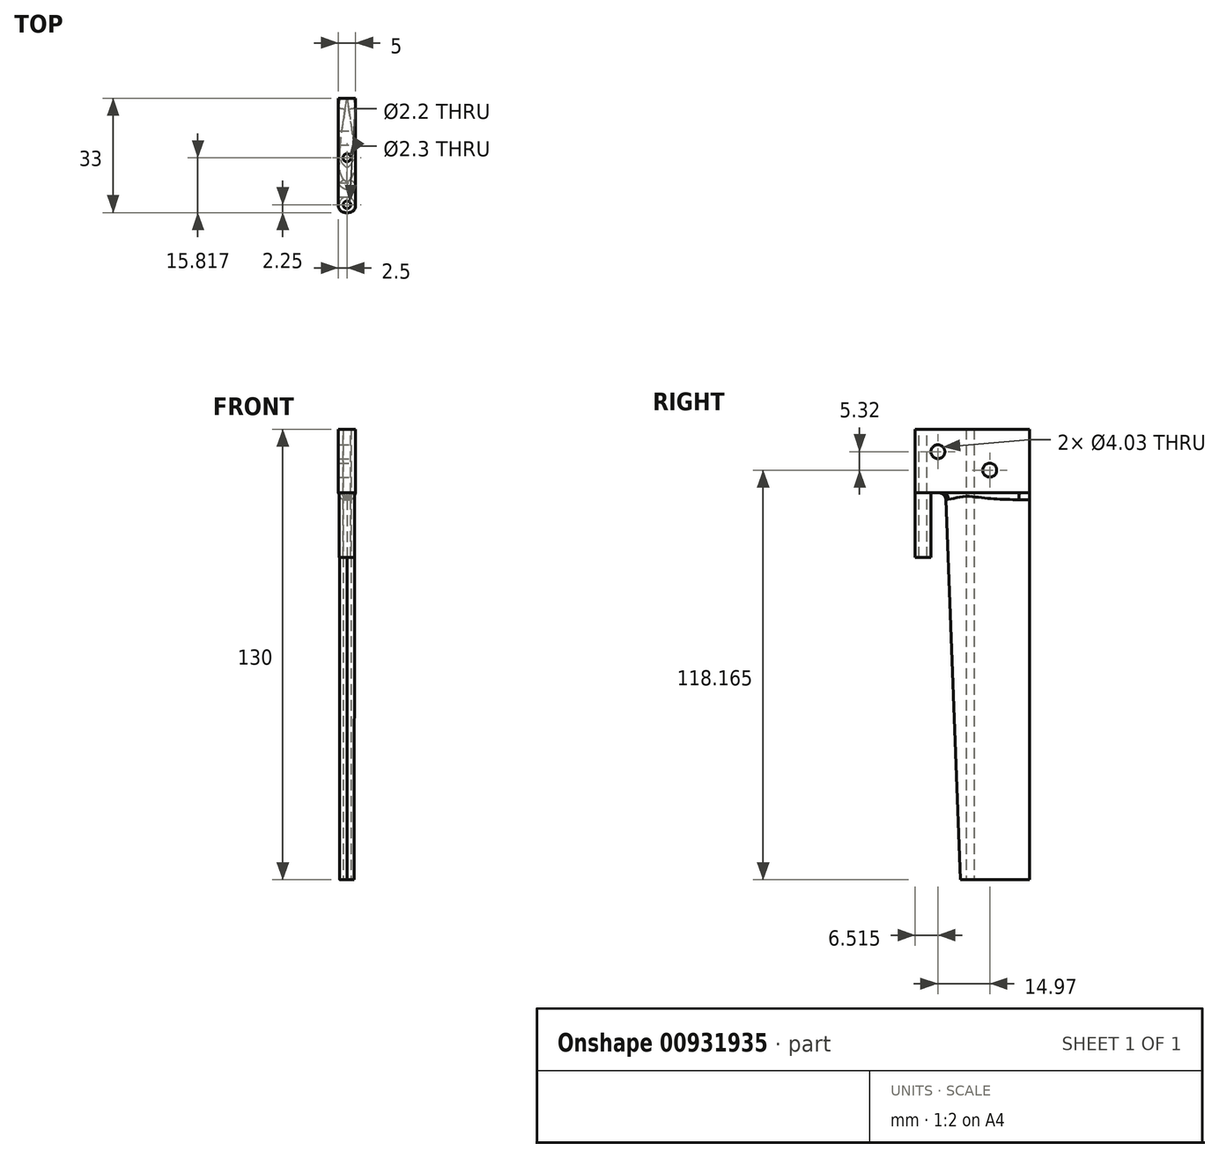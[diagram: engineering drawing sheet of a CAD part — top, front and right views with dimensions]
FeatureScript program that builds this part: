
annotation { "Feature Type Name" : "Feature", "Feature Type Description" : "" }
export const myFeature = defineFeature(function(context is Context, id is Id, definition is map)
    precondition{}
    {
        {
            var Q0;
            Q0=qCreatedBy(makeId("Top.planeOp"),FACE);
            var sketch = newSketch(context, id + "F0", { "sketchPlane" : qUnion([Q0])});
            skLineSegment(sketch, "E0", {"start": v(0, 0) * mm, "end": v(0, 20) * mm, "construction": true});
            skFitSpline(sketch, "E1", {"points": [v(0, 0) * mm, v(1.82, 2.47) * mm, v(1.18, 12.7) * mm, v(0, 20) * mm], "startDerivative": vector(9.05, 2.42) * mm, "endDerivative": vector(-3.34, 17.34) * mm});
            skFitSpline(sketch, "E2.MirrorCS", {"points": [v(0, 0) * mm, v(-1.82, 2.47) * mm, v(-1.18, 12.7) * mm, v(0, 20) * mm], "startDerivative": vector(-9.05, 2.42) * mm, "endDerivative": vector(3.34, 17.34) * mm});
            skLineSegment(sketch, "E3", {"start": v(-1.82, 2.47) * mm, "end": v(1.82, 2.47) * mm, "construction": true});
            skSolve(sketch);
        }
        {
            var Q0;
            Q0=qCreatedBy(makeId("Top.planeOp"),FACE);
            cPlane(context, id + "F1", {"entities" : qUnion([Q0]), "cplaneType" : CPlaneType.OFFSET, "offset" : 130 * mm, "width" : 150 * mm, "height" : 150 * mm});
        }
        {
            var Q0;
            Q0=qCreatedBy(id+"F1.planeOp",FACE);
            var sketch = newSketch(context, id + "F2", { "sketchPlane" : qUnion([Q0])});
            skLineSegment(sketch, "E4", {"start": v(0, 0) * mm, "end": v(0, -5) * mm, "construction": true});
            skFitSpline(sketch, "E5", {"points": [v(0, -5) * mm, v(2.11, -0.7) * mm, v(1.9, 6.2) * mm, v(0, 20) * mm], "startDerivative": vector(16.45, 7.84) * mm, "endDerivative": vector(-5.95, 33.02) * mm});
            skFitSpline(sketch, "E6.MirrorCS", {"points": [v(0, -5) * mm, v(-2.11, -0.7) * mm, v(-1.9, 6.2) * mm, v(0, 20) * mm], "startDerivative": vector(-16.45, 7.84) * mm, "endDerivative": vector(5.95, 33.02) * mm});
            skLineSegment(sketch, "E7", {"start": v(0, 0) * mm, "end": v(0, 20) * mm, "construction": true});
            skSolve(sketch);
        }
        {
            var Q0;
            Q0=qCreatedBy(id+"F1.planeOp",FACE);
            var sketch = newSketch(context, id + "F3", { "sketchPlane" : qUnion([Q0])});
            skPoint(sketch, "E8.middle", {"position": v(0, 0) * mm});
            skLineSegment(sketch, "E9", {"start": v(0, 0) * mm, "end": v(0, 20) * mm, "construction": true});
            skLineSegment(sketch, "E10", {"start": v(0, 20) * mm, "end": v(2.5, 20) * mm});
            skLineSegment(sketch, "E11", {"start": v(0, 20) * mm, "end": v(-2.5, 20) * mm});
            skLineSegment(sketch, "E12.right", {"start": v(2.5, -13) * mm, "end": v(2.5, 20) * mm});
            skLineSegment(sketch, "E13", {"start": v(-2.5, -13) * mm, "end": v(2.5, -13) * mm});
            skLineSegment(sketch, "E14", {"start": v(0, 0) * mm, "end": v(2.5, -13) * mm, "construction": true});
            skLineSegment(sketch, "E15", {"start": v(-2.5, 20) * mm, "end": v(-2.5, -13) * mm});
            skSolve(sketch);
        }
        {
            var Q0;
            Q0=makeQuery(id+"F2.imprint","IMPRINT",FACE,{"disambiguationData":[TD([[makeQuery(id+"F2.imprint","IMPRINT",EDGE,{"derivedFrom":sQuery(id+"F2.wireOp",EDGE,"E5")}),1.0]])]});
            var Q1;
            Q1=makeQuery(id+"F0.imprint","IMPRINT",FACE,{"disambiguationData":[TD([[makeQuery(id+"F0.imprint","IMPRINT",EDGE,{"derivedFrom":sQuery(id+"F0.wireOp",EDGE,"E1")}),1.0]])]});
            loft(context, id + "F4", {"sheetProfilesArray" : [{ "sheetProfileEntities" : qUnion([Q0]) }, { "sheetProfileEntities" : qUnion([Q1]) }]});
        }
        {
            var Q0;
            Q0 = qSketchRegion(id + "F3", true);
            extrude(context, id + "F5", {"entities" : qUnion([Q0]), "operationType" : NewBodyOperationType.ADD, "oppositeDirection" : true, "depth" : 18.35 * mm, "offsetDistance" : 25 * mm});
        }
        {
            var Q0;
            Q0=qCreatedBy(id+"F1.planeOp",FACE);
            var sketch = newSketch(context, id + "F6", { "sketchPlane" : qUnion([Q0])});
            skLineSegment(sketch, "E16", {"start": v(0, 0) * mm, "end": v(0, -13) * mm, "construction": true});
            skCircle(sketch, "E17", {"center": v(0, -10.75) * mm, "radius": 1.1 * mm});
            skCircle(sketch, "E18", {"center": v(0, -10.75) * mm, "radius": 2.25 * mm});
            skSolve(sketch);
        }
        {
            var Q0;
            Q0 = qSketchRegion(id + "F6", true);
            extrude(context, id + "F7", {"entities" : qUnion([Q0]), "operationType" : NewBodyOperationType.ADD, "oppositeDirection" : true, "depth" : 37 * mm, "offsetDistance" : 25 * mm});
        }
        {
            var Q0;
            Q0=makeQuery(id+"F6.imprint","IMPRINT",FACE,{"disambiguationData":[TD([[makeQuery(id+"F6.imprint","IMPRINT",EDGE,{"derivedFrom":sQuery(id+"F6.wireOp",EDGE,"E17")}),1.0]])]});
            extrude(context, id + "F8", {"entities" : qUnion([Q0]), "operationType" : NewBodyOperationType.REMOVE, "endBound" : BoundingType.SYMMETRIC, "oppositeDirection" : true, "depth" : 50 * mm, "offsetDistance" : 25 * mm});
        }
        {
            var Q0;
            Q0=qCreatedBy(makeId("Right.planeOp"),FACE);
            var sketch = newSketch(context, id + "F9", { "sketchPlane" : qUnion([Q0])});
            skLineSegment(sketch, "E19.bottom", {"start": v(-13, 111.65) * mm, "end": v(20, 111.65) * mm, "construction": true});
            skLineSegment(sketch, "E19.top", {"start": v(-13, 130) * mm, "end": v(20, 130) * mm, "construction": true});
            skLineSegment(sketch, "E19.left", {"start": v(-13, 111.65) * mm, "end": v(-13, 130) * mm, "construction": true});
            skLineSegment(sketch, "E19.right", {"start": v(20, 111.65) * mm, "end": v(20, 130) * mm, "construction": true});
            skLineSegment(sketch, "E20", {"start": v(20, 130) * mm, "end": v(15.06, 130) * mm, "construction": true});
            skCircle(sketch, "E21", {"center": v(8.48, 118.17) * mm, "radius": 2.02 * mm});
            skCircle(sketch, "E22", {"center": v(-6.49, 123.48) * mm, "radius": 2.02 * mm});
            skLineSegment(sketch, "E23", {"start": v(-6.49, 123.47) * mm, "end": v(-6.49, 123.48) * mm, "construction": true});
            skLineSegment(sketch, "E24", {"start": v(-6.49, 125.5) * mm, "end": v(-6.49, 130) * mm, "construction": true});
            skLineSegment(sketch, "E25", {"start": v(-8.5, 123.48) * mm, "end": v(-13, 123.48) * mm, "construction": true});
            skLineSegment(sketch, "E26", {"start": v(-13, 120.83) * mm, "end": v(15, 120.83) * mm, "construction": true});
            skLineSegment(sketch, "E27", {"start": v(15, 120.83) * mm, "end": v(15, 111.65) * mm, "construction": true});
            skLineSegment(sketch, "E28", {"start": v(15, 120.83) * mm, "end": v(15, 124.3) * mm, "construction": true});
            skLineSegment(sketch, "E29", {"start": v(10.5, 118.17) * mm, "end": v(15, 118.17) * mm, "construction": true});
            skSolve(sketch);
        }
        {
            var Q0;
            Q0 = qSketchRegion(id + "F9", true);
            extrude(context, id + "F10", {"entities" : qUnion([Q0]), "operationType" : NewBodyOperationType.REMOVE, "endBound" : BoundingType.SYMMETRIC, "oppositeDirection" : true, "depth" : 25 * mm, "offsetDistance" : 25 * mm});
        }
        {
            var Q0;
            {var subQ0=sQuery(id+"F2.wireOp",EDGE,"E5");var subQ1=sQuery(id+"F2.wireOp",EDGE,"E6.MirrorCS");var subQ2=sQuery(id+"F0.wireOp",EDGE,"E1");var subQ3=sQuery(id+"F0.wireOp",EDGE,"E2.MirrorCS");Q0=makeQuery(id+"F5.boolean.opBoolean","INTERSECT",EDGE,{"derivedFrom":[makeQuery(id+"F4.opLoft","SWEPT_FACE",FACE,{"disambiguationData":[OSD([subQ2,subQ3,subQ0,subQ1]),TDD([makeQuery(id+"F0.imprint","INTERSECT",VERTEX,{"disambiguationData":[OD(0.0)],"derivedFrom":[subQ2,subQ3]}),makeQuery(id+"F0.imprint","INTERSECT",VERTEX,{"disambiguationData":[OD(1.0)],"derivedFrom":[subQ2,subQ3]}),makeQuery(id+"F0.imprint","IMPRINT",EDGE,{"derivedFrom":subQ2}),makeQuery(id+"F2.imprint","INTERSECT",VERTEX,{"disambiguationData":[OD(0.0)],"derivedFrom":[subQ0,subQ1]}),makeQuery(id+"F2.imprint","INTERSECT",VERTEX,{"disambiguationData":[OD(1.0)],"derivedFrom":[subQ0,subQ1]}),makeQuery(id+"F2.imprint","IMPRINT",EDGE,{"derivedFrom":subQ0})])]}),makeQuery(id+"F5.opExtrude","CAP_FACE",FACE,{"disambiguationData":[OSD([sQuery(id+"F3.wireOp",EDGE,"E10"),sQuery(id+"F3.wireOp",EDGE,"E11"),sQuery(id+"F3.wireOp",EDGE,"E12.left"),sQuery(id+"F3.wireOp",EDGE,"E12.right"),sQuery(id+"F3.wireOp",EDGE,"E13")])],"isStart":false})]});}
            fillet(context, id + "F11", {"entities" : qUnion([Q0]), "radius" : 2 * mm, "tangentPropagation" : true, "allowEdgeOverflow" : false});
        }
        {
            var Q0;
            {var subQ0=sQuery(id+"F2.wireOp",EDGE,"E6.MirrorCS");var subQ1=sQuery(id+"F2.wireOp",EDGE,"E5");var subQ2=sQuery(id+"F0.wireOp",EDGE,"E2.MirrorCS");var subQ3=sQuery(id+"F0.wireOp",EDGE,"E1");Q0=makeQuery(id+"F5.boolean.opBoolean","INTERSECT",EDGE,{"derivedFrom":[makeQuery(id+"F4.opLoft","SWEPT_FACE",FACE,{"disambiguationData":[OSD([subQ3,subQ2,subQ1,subQ0]),TDD([makeQuery(id+"F0.imprint","INTERSECT",VERTEX,{"disambiguationData":[OD(0.0)],"derivedFrom":[subQ3,subQ2]}),makeQuery(id+"F0.imprint","INTERSECT",VERTEX,{"disambiguationData":[OD(1.0)],"derivedFrom":[subQ3,subQ2]}),makeQuery(id+"F0.imprint","IMPRINT",EDGE,{"derivedFrom":subQ2}),makeQuery(id+"F2.imprint","INTERSECT",VERTEX,{"disambiguationData":[OD(0.0)],"derivedFrom":[subQ1,subQ0]}),makeQuery(id+"F2.imprint","INTERSECT",VERTEX,{"disambiguationData":[OD(1.0)],"derivedFrom":[subQ1,subQ0]}),makeQuery(id+"F2.imprint","IMPRINT",EDGE,{"derivedFrom":subQ0})])]}),makeQuery(id+"F5.opExtrude","CAP_FACE",FACE,{"disambiguationData":[OSD([sQuery(id+"F3.wireOp",EDGE,"E10"),sQuery(id+"F3.wireOp",EDGE,"E11"),sQuery(id+"F3.wireOp",EDGE,"E12.left"),sQuery(id+"F3.wireOp",EDGE,"E12.right"),sQuery(id+"F3.wireOp",EDGE,"E13")])],"isStart":false})]});}
            fillet(context, id + "F12", {"entities" : qUnion([Q0]), "radius" : 2 * mm, "tangentPropagation" : true, "allowEdgeOverflow" : false});
        }
        {
            var Q0;
            Q0=qCreatedBy(makeId("Top.planeOp"),FACE);
            var sketch = newSketch(context, id + "F13", { "sketchPlane" : qUnion([Q0])});
            skCircle(sketch, "E30", {"center": v(0, 2.82) * mm, "radius": 1.15 * mm});
            skSolve(sketch);
        }
        {
            var Q0;
            Q0 = qSketchRegion(id + "F13", true);
            extrude(context, id + "F14", {"entities" : qUnion([Q0]), "operationType" : NewBodyOperationType.REMOVE, "depth" : 140 * mm, "offsetDistance" : 25 * mm});
        }
        {
            var Q0;
            Q0=makeQuery(id+"F5.opExtrude","SWEPT_EDGE",EDGE,{"disambiguationData":[OSD([sQuery(id+"F3.wireOp",EDGE,"E12.left"),sQuery(id+"F3.wireOp",EDGE,"E13")])]});
            var Q1;
            Q1=makeQuery(id+"F5.opExtrude","SWEPT_EDGE",EDGE,{"disambiguationData":[OSD([sQuery(id+"F3.wireOp",EDGE,"E12.right"),sQuery(id+"F3.wireOp",EDGE,"E13")])]});
            fillet(context, id + "F15", {"entities" : qUnion([Q0, Q1]), "radius" : 2 * mm, "tangentPropagation" : true, "allowEdgeOverflow" : false});
        }
    });
